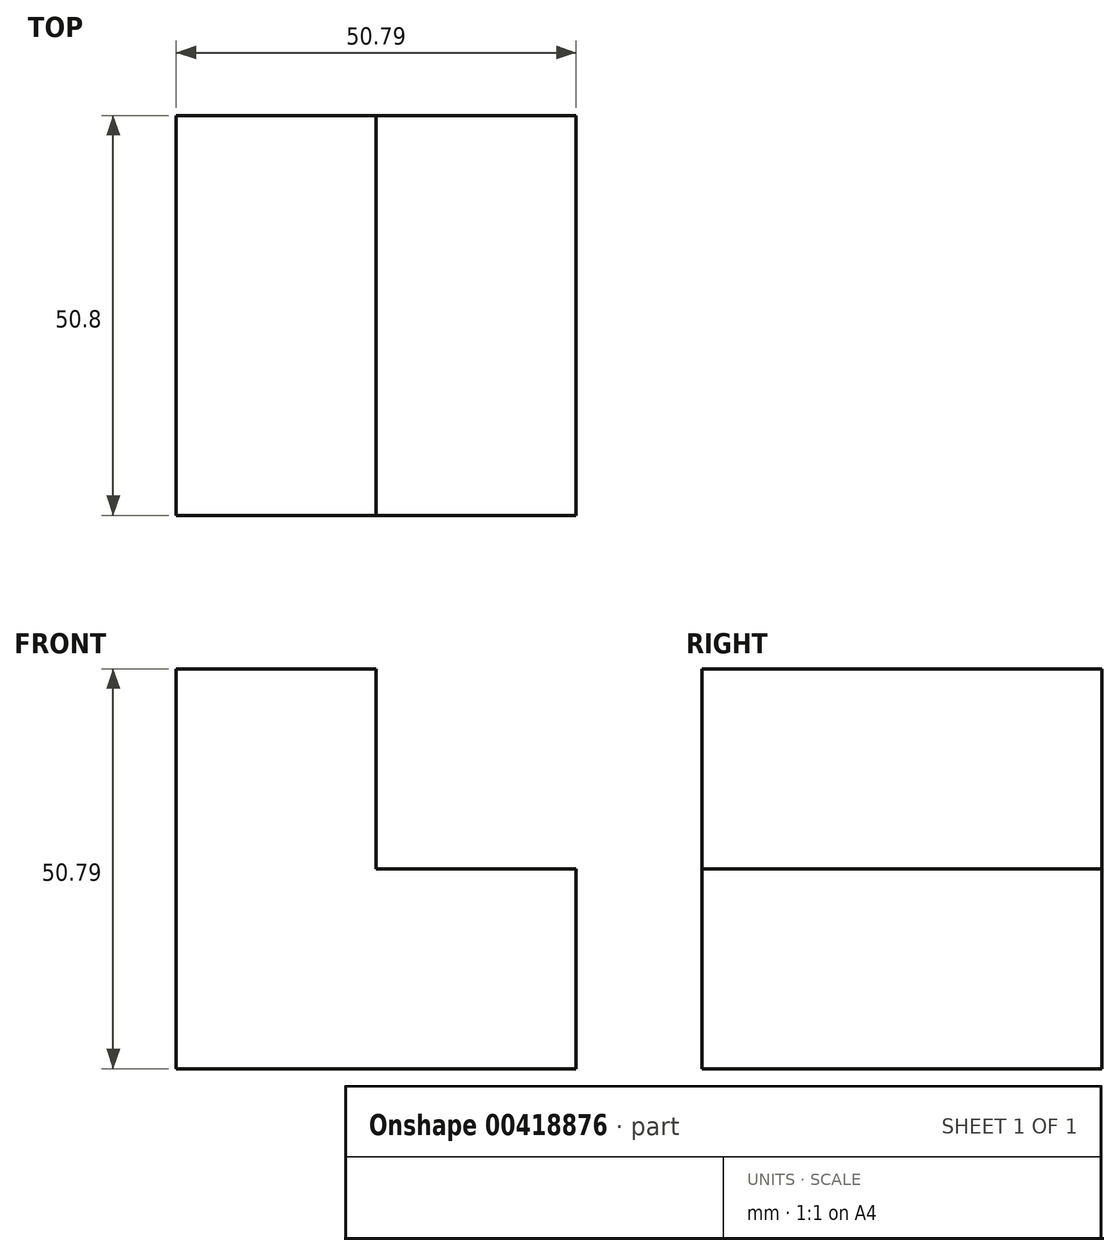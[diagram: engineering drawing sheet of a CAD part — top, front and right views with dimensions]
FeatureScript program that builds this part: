
annotation { "Feature Type Name" : "Feature", "Feature Type Description" : "" }
export const myFeature = defineFeature(function(context is Context, id is Id, definition is map)
    precondition{}
    {
        {
            var Q0;
            Q0=qCreatedBy(makeId("Front.planeOp"),FACE);
            var sketch = newSketch(context, id + "F0", { "sketchPlane" : qUnion([Q0])});
            skLineSegment(sketch, "E0", {"start": v(0, 0) * mm, "end": v(-50.8, 0) * mm});
            skLineSegment(sketch, "E1", {"start": v(-50.8, 0) * mm, "end": v(-50.8, 50.8) * mm});
            skLineSegment(sketch, "E2", {"start": v(-50.8, 50.8) * mm, "end": v(-25.4, 50.8) * mm});
            skLineSegment(sketch, "E3", {"start": v(-25.4, 50.8) * mm, "end": v(-25.4, 25.4) * mm});
            skLineSegment(sketch, "E4", {"start": v(-25.4, 25.4) * mm, "end": v(0, 25.4) * mm});
            skLineSegment(sketch, "E5", {"start": v(0, 25.4) * mm, "end": v(0, 0) * mm});
            skSolve(sketch);
        }
        {
            var Q0;
            Q0 = qSketchRegion(id + "F0", true);
            var Q1;
            Q1=makeQuery(id+"F0.imprint","IMPRINT",FACE,{"disambiguationData":[TD([[makeQuery(id+"F0.imprint","IMPRINT",EDGE,{"derivedFrom":sQuery(id+"F0.wireOp",EDGE,"E0")}),-1.0]])]});
            extrude(context, id + "F1", {"entities" : qUnion([Q0, Q1]), "depth" : 50.8 * mm});
        }
    });
